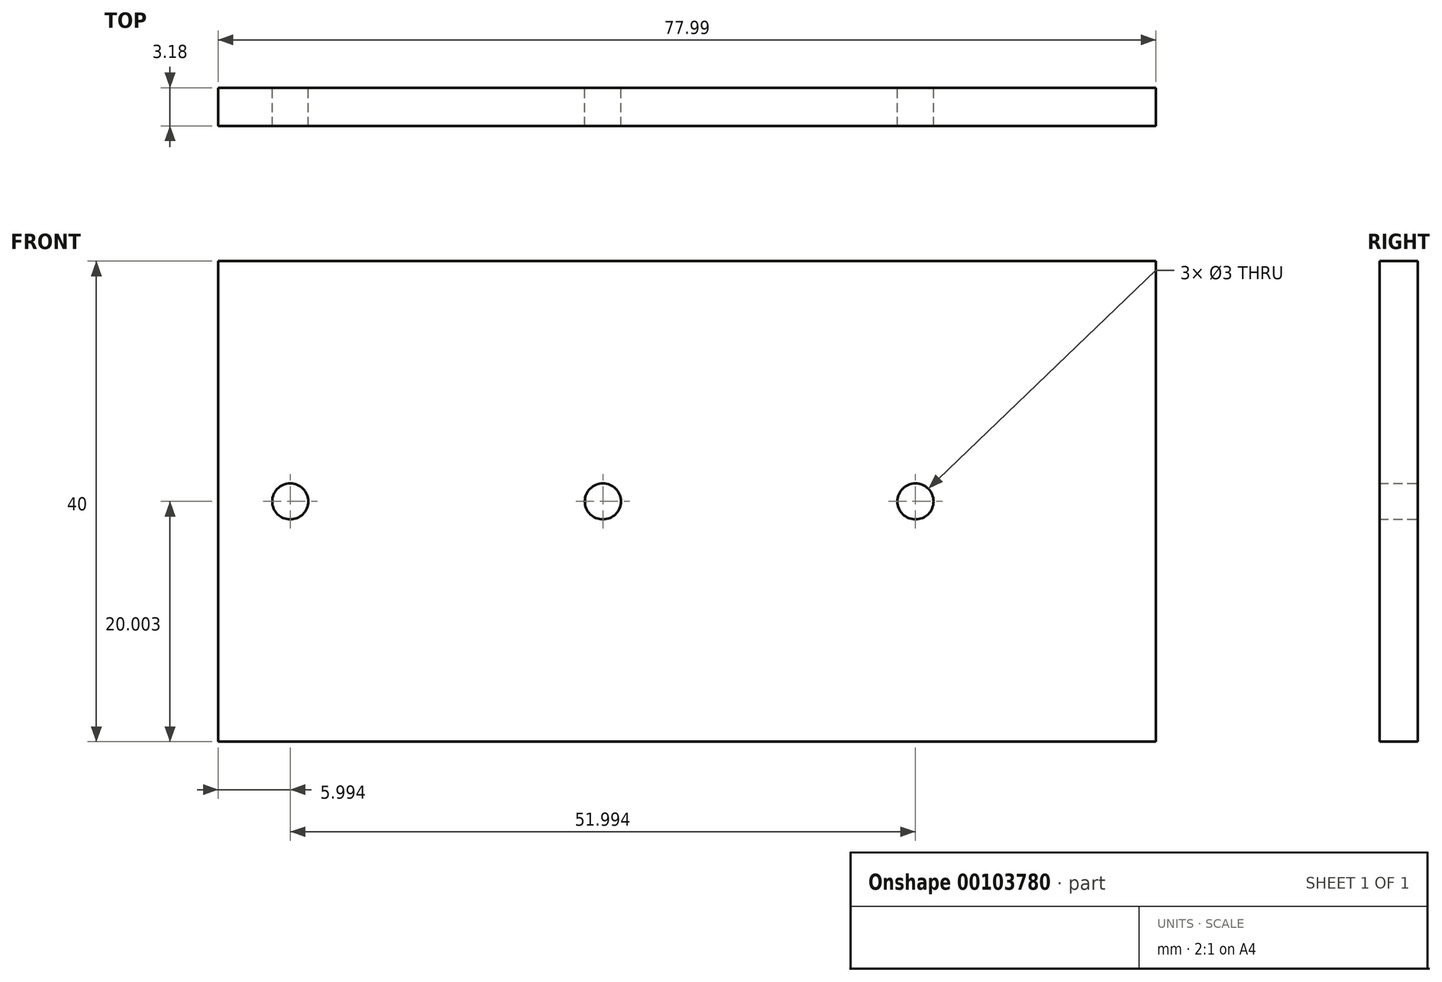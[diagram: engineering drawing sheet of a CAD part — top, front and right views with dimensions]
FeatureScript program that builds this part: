
annotation { "Feature Type Name" : "Feature", "Feature Type Description" : "" }
export const myFeature = defineFeature(function(context is Context, id is Id, definition is map)
    precondition{}
    {
        {
            var Q0;
            Q0=qCreatedBy(makeId("Front.planeOp"),FACE);
            var sketch = newSketch(context, id + "F0", { "sketchPlane" : qUnion([Q0])});
            skLineSegment(sketch, "E0.bottom", {"start": v(0, 0) * mm, "end": v(78, 0) * mm});
            skLineSegment(sketch, "E0.top", {"start": v(0, 40) * mm, "end": v(78, 40) * mm});
            skLineSegment(sketch, "E0.left", {"start": v(0, 0) * mm, "end": v(0, 40) * mm});
            skLineSegment(sketch, "E0.right", {"start": v(78, 0) * mm, "end": v(78, 40) * mm});
            skLineSegment(sketch, "E1", {"start": v(0, 20) * mm, "end": v(6, 20) * mm});
            skPoint(sketch, "E1.endSnap0", {"position": v(0, 20) * mm});
            skLineSegment(sketch, "E2", {"start": v(6, 20) * mm, "end": v(32, 20) * mm});
            skLineSegment(sketch, "E3", {"start": v(32, 20) * mm, "end": v(57.99, 20) * mm});
            skCircle(sketch, "E4", {"center": v(6, 20) * mm, "radius": 1.5 * mm});
            skCircle(sketch, "E5", {"center": v(32, 20) * mm, "radius": 1.5 * mm});
            skCircle(sketch, "E6", {"center": v(57.99, 20) * mm, "radius": 1.5 * mm});
            skLineSegment(sketch, "E7", {"start": v(32, 20) * mm, "end": v(32, 8.58) * mm});
            skLineSegment(sketch, "E8", {"start": v(32, 8.58) * mm, "end": v(6, 8.58) * mm});
            skPoint(sketch, "E9.orphan", {"position": v(32, 0) * mm});
            skSolve(sketch);
        }
        {
            var Q0;
            {var subQ7=sQuery(id+"F0.wireOp",EDGE,"E0.bottom");Q0=makeQuery(id+"F0.imprint","IMPRINT",FACE,{"disambiguationData":[TD([[makeQuery(id+"F0.imprint","IMPRINT",EDGE,{"derivedFrom":subQ7}),1.0]])]});}
            extrude(context, id + "F1", {"entities" : qUnion([Q0]), "depth" : 3.17 * mm});
        }
    });
